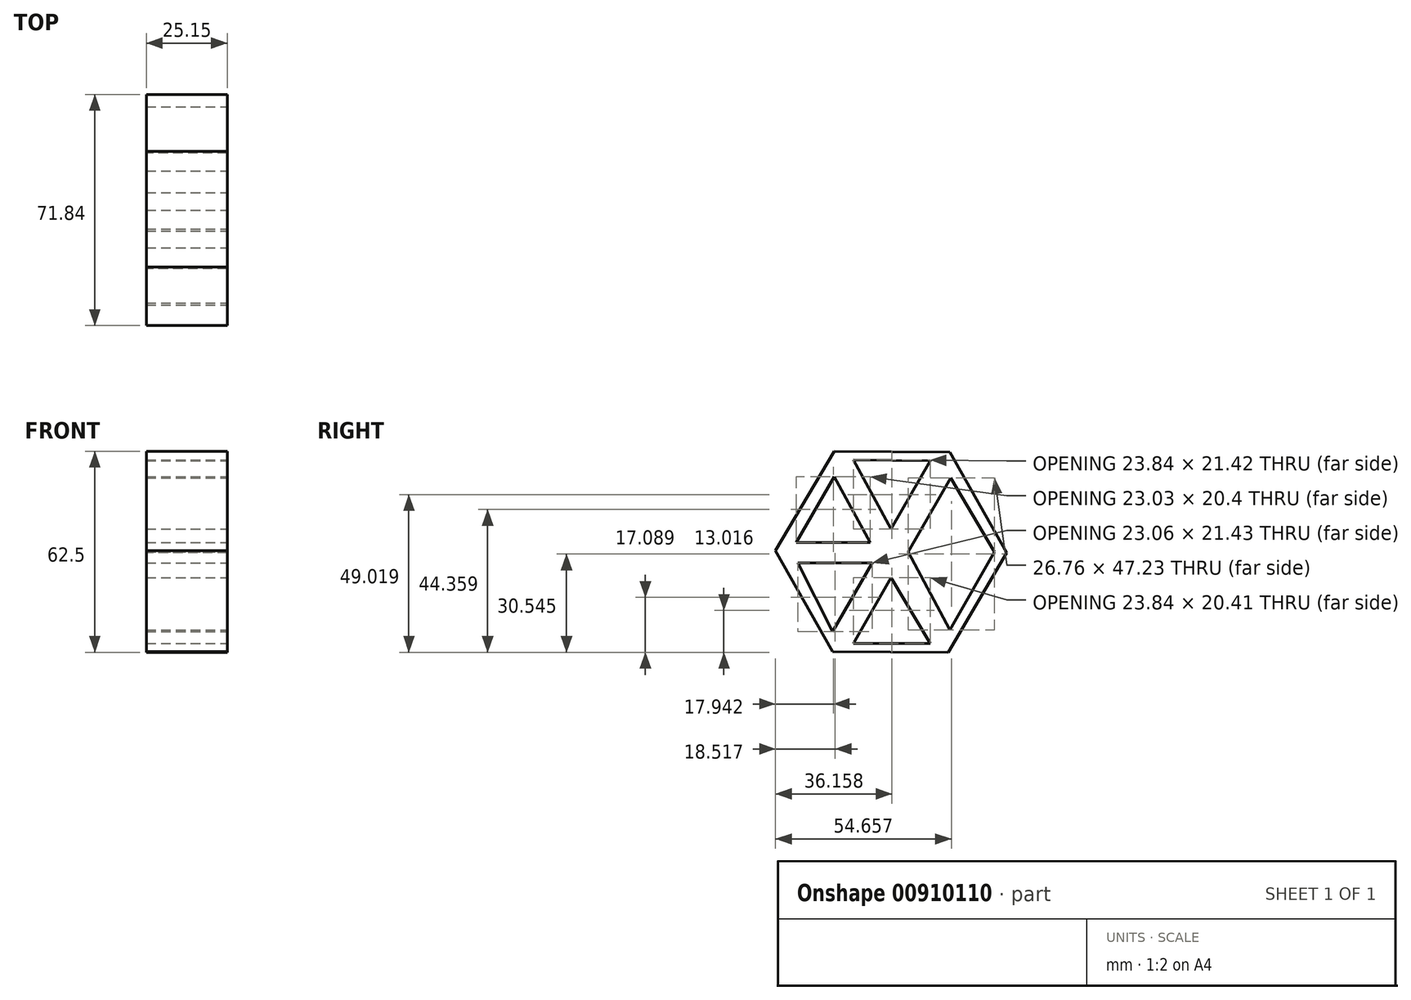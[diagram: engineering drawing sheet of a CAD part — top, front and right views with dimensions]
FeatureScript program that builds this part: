
annotation { "Feature Type Name" : "Feature", "Feature Type Description" : "" }
export const myFeature = defineFeature(function(context is Context, id is Id, definition is map)
    precondition{}
    {
        {
            var Q0;
            Q0=qCreatedBy(makeId("Right.planeOp"),FACE);
            var sketch = newSketch(context, id + "F0", { "sketchPlane" : qUnion([Q0])});
            skCircle(sketch, "E0.cCircle", {"center": v(0, 0) * mm, "radius": 31.11 * mm, "construction": true});
            skLineSegment(sketch, "E0.0", {"start": v(17.73, -31.25) * mm, "end": v(-18.2, -30.98) * mm});
            skLineSegment(sketch, "E0.1", {"start": v(-18.2, -30.98) * mm, "end": v(-35.92, 0.27) * mm});
            skLineSegment(sketch, "E0.2", {"start": v(-35.92, 0.27) * mm, "end": v(-17.73, 31.25) * mm});
            skLineSegment(sketch, "E0.3", {"start": v(-17.73, 31.25) * mm, "end": v(18.2, 30.98) * mm});
            skLineSegment(sketch, "E0.4", {"start": v(18.2, 30.98) * mm, "end": v(35.92, -0.27) * mm});
            skLineSegment(sketch, "E0.5", {"start": v(35.92, -0.27) * mm, "end": v(17.73, -31.25) * mm});
            skPoint(sketch, "E0.0.midPoint", {"position": v(-0.23, -31.11) * mm});
            skSolve(sketch);
        }
        {
            var Q0;
            Q0=makeQuery(id+"F0.imprint","IMPRINT",FACE,{"disambiguationData":[TD([[makeQuery(id+"F0.imprint","IMPRINT",EDGE,{"derivedFrom":sQuery(id+"F0.wireOp",EDGE,"E0.0")}),-1.0]])]});
            extrude(context, id + "F1", {"entities" : qUnion([Q0]), "depth" : 25.15 * mm, "offsetDistance" : 25.4 * mm});
        }
        {
            var Q0;
            Q0=makeQuery(id+"F1.opExtrude","CAP_FACE",FACE,{"disambiguationData":[OSD([sQuery(id+"F0.wireOp",EDGE,"E0.0"),sQuery(id+"F0.wireOp",EDGE,"E0.1"),sQuery(id+"F0.wireOp",EDGE,"E0.2"),sQuery(id+"F0.wireOp",EDGE,"E0.3"),sQuery(id+"F0.wireOp",EDGE,"E0.4"),sQuery(id+"F0.wireOp",EDGE,"E0.5")])],"isStart":false});
            var sketch = newSketch(context, id + "F2", { "sketchPlane" : qUnion([Q0])});
            skLineSegment(sketch, "E1", {"start": v(-17.7, 23.3) * mm, "end": v(-29.5, 2.91) * mm});
            skLineSegment(sketch, "E2", {"start": v(-17.7, 23.3) * mm, "end": v(-6.47, 2.91) * mm});
            skLineSegment(sketch, "E3", {"start": v(-29.5, 2.91) * mm, "end": v(-6.47, 2.91) * mm});
            skLineSegment(sketch, "E4", {"start": v(-28.93, -3.44) * mm, "end": v(-5.87, -3.44) * mm});
            skLineSegment(sketch, "E5", {"start": v(-5.87, -3.44) * mm, "end": v(-18.2, -24.88) * mm});
            skLineSegment(sketch, "E6", {"start": v(-28.93, -3.44) * mm, "end": v(-18.2, -24.88) * mm});
            skLineSegment(sketch, "E7", {"start": v(0, -8.03) * mm, "end": v(-11.68, -28.44) * mm});
            skLineSegment(sketch, "E8", {"start": v(12.16, -28.44) * mm, "end": v(-11.68, -28.44) * mm});
            skLineSegment(sketch, "E9", {"start": v(0, -8.03) * mm, "end": v(12.16, -28.44) * mm});
            skLineSegment(sketch, "E10", {"start": v(5.36, 0) * mm, "end": v(18.47, 22.9) * mm});
            skLineSegment(sketch, "E11", {"start": v(18.47, 22.9) * mm, "end": v(32.12, 0) * mm});
            skLineSegment(sketch, "E12", {"start": v(32.12, 0) * mm, "end": v(18.2, -24.32) * mm});
            skLineSegment(sketch, "E13", {"start": v(5.36, 0) * mm, "end": v(18.2, -24.32) * mm});
            skLineSegment(sketch, "E14", {"start": v(-11.68, 28.48) * mm, "end": v(12.16, 28.3) * mm});
            skLineSegment(sketch, "E15", {"start": v(12.16, 28.3) * mm, "end": v(0, 7.06) * mm});
            skLineSegment(sketch, "E16", {"start": v(0, 7.06) * mm, "end": v(-11.68, 28.48) * mm});
            skSolve(sketch);
        }
        {
            var Q0;
            Q0=makeQuery(id+"F2.imprint","IMPRINT",FACE,{"disambiguationData":[TD([[makeQuery(id+"F2.imprint","IMPRINT",EDGE,{"derivedFrom":sQuery(id+"F2.wireOp",EDGE,"E14")}),-1.0]])]});
            var Q1;
            Q1=makeQuery(id+"F2.imprint","IMPRINT",FACE,{"disambiguationData":[TD([[makeQuery(id+"F2.imprint","IMPRINT",EDGE,{"derivedFrom":sQuery(id+"F2.wireOp",EDGE,"E10")}),-1.0]])]});
            var Q2;
            Q2=makeQuery(id+"F2.imprint","IMPRINT",FACE,{"disambiguationData":[TD([[makeQuery(id+"F2.imprint","IMPRINT",EDGE,{"derivedFrom":sQuery(id+"F2.wireOp",EDGE,"E7")}),1.0]])]});
            var Q3;
            Q3=makeQuery(id+"F2.imprint","IMPRINT",FACE,{"disambiguationData":[TD([[makeQuery(id+"F2.imprint","IMPRINT",EDGE,{"derivedFrom":sQuery(id+"F2.wireOp",EDGE,"E4")}),-1.0]])]});
            var Q4;
            Q4=makeQuery(id+"F2.imprint","IMPRINT",FACE,{"disambiguationData":[TD([[makeQuery(id+"F2.imprint","IMPRINT",EDGE,{"derivedFrom":sQuery(id+"F2.wireOp",EDGE,"E1")}),1.0]])]});
            extrude(context, id + "F3", {"entities" : qUnion([Q0, Q1, Q2, Q3, Q4]), "operationType" : NewBodyOperationType.REMOVE, "endBound" : BoundingType.THROUGH_ALL, "oppositeDirection" : true, "depth" : 25.4 * mm, "offsetDistance" : 25.4 * mm});
        }
    });
